# Revit family: Hager-Univers-IP30-D161-Cl.II-FWB-encl--NoHosted-CH-it
name_source: partatom
category: Electrical Equipment
units: mm (PartAtom-declared; Revit-internal decimal feet)

## family parameters
Always vertical = Yes
Cut with Voids When Loaded = No
Panel Configuration = Two Columns, Circuits Across
Part Type = Panelboard
Room Calculation Point = No
Round Connector Dimension = Use Diameter
Shared = No
Work Plane-Based = Yes

## types (19) — shared parameters
Default Elevation = 1219 mm
EF000003 - Tipo di montaggio = EV000384 - A parete
EF000007 - colore = EV000202 - bianco
EF000049 - profondità = 161 mm  [stored 0.528215 ft]
EF000116 - numero RAL = 9010
EF000118 - con piastra di montaggio = No
EF001088 - possibilità di applicazione = Yes
EF001596 - Attacco Lampada = EV000179 - acciaio
EF001613 - Integrità del circuito = EV000494 - senza
EF002950 - Numero moduli DIN = 12
EF003532 - adatto per uso esterno = No
EF004293 - resistenza agli urti = EV006815 - IK09
EF004464 - tipo di porta = EV000494 - senza
EF005474 - grado di protezione (IP) = EV006410 - IP30
EF006244 - coperchio/porta trasparente = No
EF006306 - con serratura = No
EF007800 - adatto per parafulmine = No
EF008873 - corrente nominale (In) = 125 A
EF015940 - Coprire con rilascio di sovrapressione = No
HG000002 - Con porta = No
HG000003 - Gamma = Univers
HG000006 - Ad incasso = No
HG000009 - Porta doppia a battente = No
HG000010 - Porte asimmetriche = No
HG000023 - Custodia a doppia sezione = No
HG000024 - Altezza della sezione inferiore = 600 mm
HG000026 - A pavimento = No
Manufacturer = Hager
Type Comments = Univers
zero-valued in all types: EF000218 - profondità di incasso, EF000266 - numero di file, HG000027 - Altezza dello zoccolo

## per-type parameters (varying)
| type | EF000008 - Larghezza | EF000040 - Altezza | EF000339 - tipo di copertura | EF000437 - numero di ingressi per conduttori | EF001131 - profondità interna | EF004427 - numero di moduli | EF009170 - spessore materiale scatola | EF009171 - spessore materiale porta/coperchio | EF009212 - esecuzione coperchio | EF009554 - numero delle aperture per la piastra della flangia | HG000004 - Codice produttore |
| A parete IP30 L1050 A1100 P161  - FWB74D1 | 1050 mm | 1100 mm | EV000494 - senza | 16 | 156 mm  [stored 0.511811 ft] | 336 | 1 mm  [stored 0.00328084 ft] | 1 mm  [stored 0.00328084 ft] | EV009916 - con taglio | 8 | FWB74D1 |
| A parete IP30 L1050 A500 P161  - FWB34D1 | 1050 mm | 500 mm  [stored 1.64042 ft] | EV000494 - senza | 16 | 156 mm  [stored 0.511811 ft] | 144 | 1 mm  [stored 0.00328084 ft] | 2 mm  [stored 0.00656168 ft] | EV009916 - con taglio | 8 | FWB34D1 |
| A parete IP30 L1050 A650 P161  - FWB44D1 | 1050 mm | 650 mm  [stored 2.13255 ft] | EV004216 - porta | 16 | 160 mm  [stored 0.524934 ft] | 192 | 1 mm  [stored 0.00328084 ft] | 1 mm  [stored 0.00328084 ft] | EV000116 - chiuso | 8 | FWB44D1 |
| A parete IP30 L1050 A800 P161  - FWB54D1 | 1050 mm | 800 mm  [stored 2.62467 ft] | EV004216 - porta | 16 | 160 mm  [stored 0.524934 ft] | 240 | 2 mm  [stored 0.00656168 ft] | 1 mm  [stored 0.00328084 ft] | EV009916 - con taglio | 8 | FWB54D1 |
| A parete IP30 L1050 A950 P161  - FWB64D1 | 1050 mm | 950 mm  [stored 3.1168 ft] | EV004216 - porta | 16 | 160 mm  [stored 0.524934 ft] | 288 | 2 mm  [stored 0.00656168 ft] | 1 mm  [stored 0.00328084 ft] | EV009916 - con taglio | 8 | FWB64D1 |
| A parete IP30 L300 A1100 P161  - FWB71D1 | 300 mm | 1100 mm | EV000494 - senza | 4 | 156 mm  [stored 0.511811 ft] | 84 | 1 mm  [stored 0.00328084 ft] | 1 mm  [stored 0.00328084 ft] | EV009916 - con taglio | 2 | FWB71D1 |
| A parete IP30 L300 A1250 P161  - FWB81D1 | 300 mm | 1250 mm  [stored 4.10105 ft] | EV000494 - senza | 4 | 160 mm  [stored 0.524934 ft] | 96 | 1 mm  [stored 0.00328084 ft] | 1 mm  [stored 0.00328084 ft] | EV009916 - con taglio | 2 | FWB81D1 |
| A parete IP30 L300 A650 P161  - FWB41D1 | 300 mm | 650 mm  [stored 2.13255 ft] | EV004216 - porta | 4 | 160 mm  [stored 0.524934 ft] | 48 | 1 mm  [stored 0.00328084 ft] | 1 mm  [stored 0.00328084 ft] | EV000116 - chiuso | 2 | FWB41D1 |
| A parete IP30 L300 A800 P161  - FWB51D1 | 300 mm | 800 mm  [stored 2.62467 ft] | EV000494 - senza | 4 | 156 mm  [stored 0.511811 ft] | 60 | 1 mm  [stored 0.00328084 ft] | 1 mm  [stored 0.00328084 ft] | EV009916 - con taglio | 2 | FWB51D1 |
| A parete IP30 L300 A950 P161  - FWB61D1 | 300 mm | 950 mm  [stored 3.1168 ft] | EV000494 - senza | 4 | 156 mm  [stored 0.511811 ft] | 72 | 1 mm  [stored 0.00328084 ft] | 1 mm  [stored 0.00328084 ft] | EV009916 - con taglio | 2 | FWB61D1 |
| A parete IP30 L550 A1100 P161  - FWB72D1 | 550 mm | 1100 mm | EV000494 - senza | 8 | 156 mm  [stored 0.511811 ft] | 168 | 1 mm  [stored 0.00328084 ft] | 1 mm  [stored 0.00328084 ft] | EV009916 - con taglio | 4 | FWB72D1 |
| A parete IP30 L550 A500 P161  - FWB32D1 | 550 mm | 500 mm  [stored 1.64042 ft] | EV000494 - senza | 8 | 156 mm  [stored 0.511811 ft] | 72 | 2 mm  [stored 0.00656168 ft] | 2 mm  [stored 0.00656168 ft] | EV009916 - con taglio | 4 | FWB32D1 |
| A parete IP30 L550 A650 P161  - FWB42D1 | 550 mm | 650 mm  [stored 2.13255 ft] | EV004216 - porta | 8 | 160 mm  [stored 0.524934 ft] | 96 | 1 mm  [stored 0.00328084 ft] | 1 mm  [stored 0.00328084 ft] | EV000116 - chiuso | 4 | FWB42D1 |
| A parete IP30 L550 A800 P161  - FWB52D1 | 550 mm | 800 mm  [stored 2.62467 ft] | EV000494 - senza | 8 | 156 mm  [stored 0.511811 ft] | 120 | 1 mm  [stored 0.00328084 ft] | 1 mm  [stored 0.00328084 ft] | EV009916 - con taglio | 4 | FWB52D1 |
| A parete IP30 L550 A950 P161  - FWB62D1 | 550 mm | 950 mm  [stored 3.1168 ft] | EV000494 - senza | 8 | 156 mm  [stored 0.511811 ft] | 144 | 1 mm  [stored 0.00328084 ft] | 1 mm  [stored 0.00328084 ft] | EV009916 - con taglio | 4 | FWB62D1 |
| A parete IP30 L800 A500 P161  - FWB33D1 | 800 mm  [stored 2.62467 ft] | 500 mm  [stored 1.64042 ft] | EV004216 - porta | 12 | 160 mm  [stored 0.524934 ft] | 108 | 1 mm  [stored 0.00328084 ft] | 1 mm  [stored 0.00328084 ft] | EV000116 - chiuso | 6 | FWB33D1 |
| A parete IP30 L800 A650 P161  - FWB43D1 | 800 mm  [stored 2.62467 ft] | 650 mm  [stored 2.13255 ft] | EV004216 - porta | 12 | 160 mm  [stored 0.524934 ft] | 144 | 2 mm  [stored 0.00656168 ft] | 1 mm  [stored 0.00328084 ft] | EV000116 - chiuso | 6 | FWB43D1 |
| A parete IP30 L800 A800 P161  - FWB53D1 | 800 mm  [stored 2.62467 ft] | 800 mm  [stored 2.62467 ft] | EV004216 - porta | 12 | 160 mm  [stored 0.524934 ft] | 180 | 1 mm  [stored 0.00328084 ft] | 1 mm  [stored 0.00328084 ft] | EV000116 - chiuso | 6 | FWB53D1 |
| A parete IP30 L800 A950 P161  - FWB63D1 | 800 mm  [stored 2.62467 ft] | 950 mm  [stored 3.1168 ft] | EV004216 - porta | 12 | 160 mm  [stored 0.524934 ft] | 216 | 2 mm  [stored 0.00656168 ft] | 1 mm  [stored 0.00328084 ft] | EV009916 - con taglio | 6 | FWB63D1 |

note: [stored X ft] marks values corroborated as IEEE doubles in the binary element streams (Revit-internal decimal feet)

## geometry (parser evidence)
native form markers: Blend x4, Sweep x10
no freeform markers — native parametric forms only
